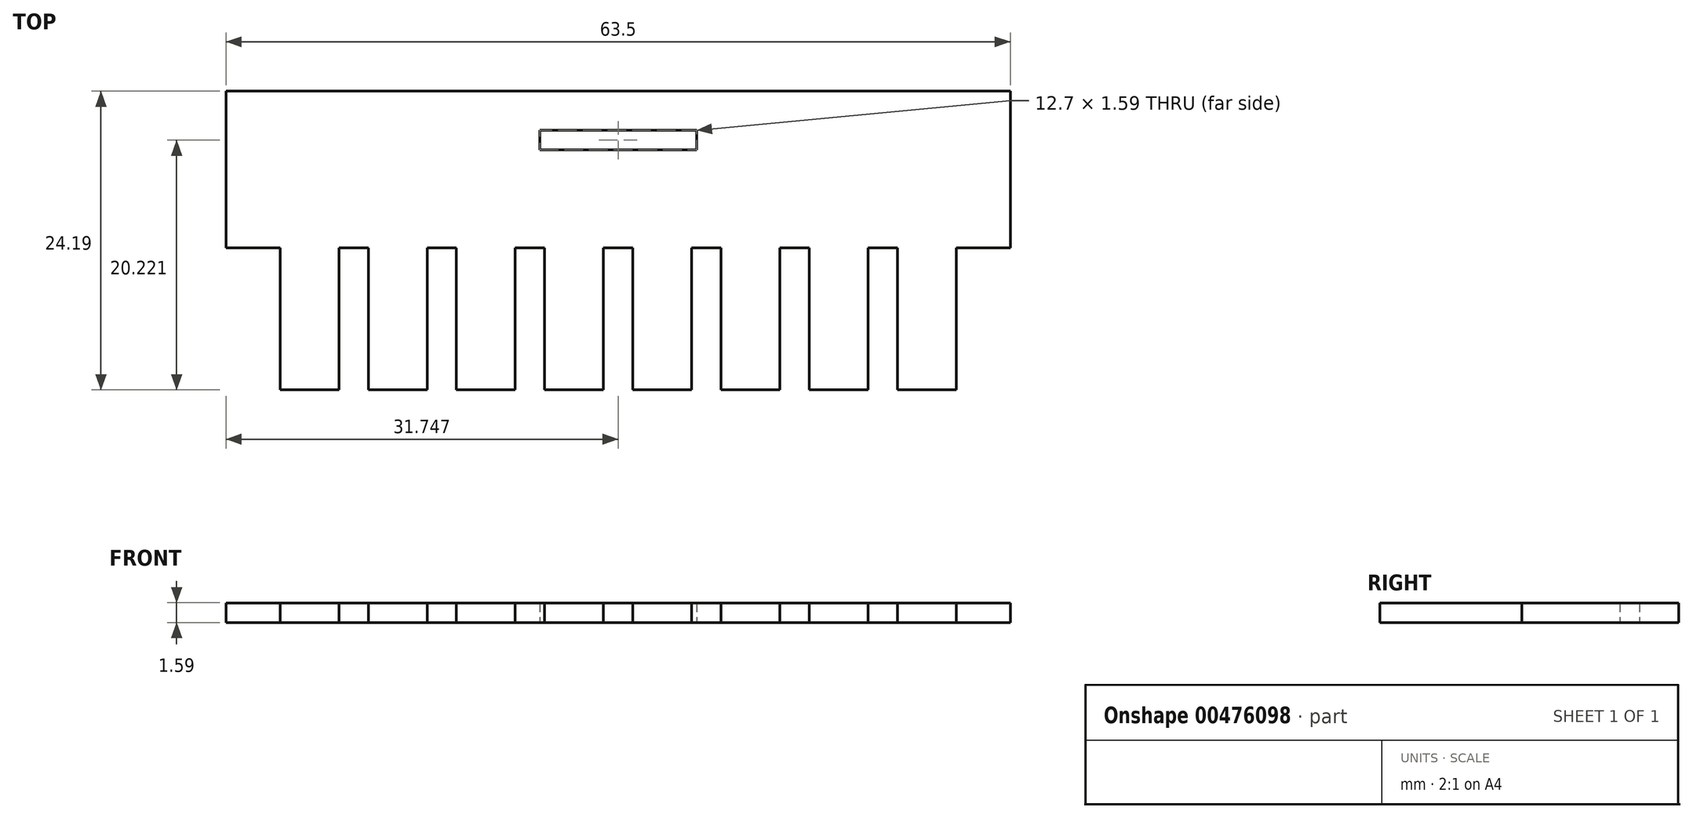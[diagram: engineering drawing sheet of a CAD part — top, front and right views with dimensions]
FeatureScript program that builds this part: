
annotation { "Feature Type Name" : "Feature", "Feature Type Description" : "" }
export const myFeature = defineFeature(function(context is Context, id is Id, definition is map)
    precondition{}
    {
        {
            var Q0;
            Q0=qCreatedBy(makeId("Top.planeOp"),FACE);
            var sketch = newSketch(context, id + "F0", { "sketchPlane" : qUnion([Q0])});
            skLineSegment(sketch, "E0.top", {"start": v(31.74, 14.04) * mm, "end": v(-31.76, 14.04) * mm});
            skPoint(sketch, "E0.middle", {"position": v(0, 0) * mm});
            skLineSegment(sketch, "E1", {"start": v(-27.38, 1.34) * mm, "end": v(-27.38, -10.15) * mm});
            skLineSegment(sketch, "E2", {"start": v(27.36, 1.34) * mm, "end": v(27.36, -10.15) * mm});
            skLineSegment(sketch, "E3", {"start": v(31.74, 14.04) * mm, "end": v(31.74, 1.34) * mm});
            skLineSegment(sketch, "E4", {"start": v(-31.76, 14.04) * mm, "end": v(-31.76, 1.34) * mm});
            skLineSegment(sketch, "E5", {"start": v(-31.76, 1.34) * mm, "end": v(-27.38, 1.34) * mm});
            skLineSegment(sketch, "E6", {"start": v(27.36, 1.34) * mm, "end": v(31.74, 1.34) * mm});
            skLineSegment(sketch, "E7", {"start": v(-27.38, -10.15) * mm, "end": v(-22.62, -10.15) * mm});
            skLineSegment(sketch, "E8", {"start": v(-22.62, -10.15) * mm, "end": v(-22.62, 1.34) * mm});
            skLineSegment(sketch, "E9", {"start": v(-22.62, 1.34) * mm, "end": v(-20.24, 1.34) * mm});
            skLineSegment(sketch, "E10", {"start": v(-20.24, 1.34) * mm, "end": v(-20.24, -10.15) * mm});
            skLineSegment(sketch, "E11", {"start": v(-20.24, -10.15) * mm, "end": v(-15.48, -10.15) * mm});
            skLineSegment(sketch, "E12", {"start": v(-15.48, -10.15) * mm, "end": v(-15.48, 1.34) * mm});
            skLineSegment(sketch, "E13", {"start": v(-15.48, 1.34) * mm, "end": v(-13.1, 1.34) * mm});
            skLineSegment(sketch, "E14", {"start": v(-13.1, 1.34) * mm, "end": v(-13.1, -10.15) * mm});
            skLineSegment(sketch, "E15", {"start": v(-13.1, -10.15) * mm, "end": v(-8.34, -10.15) * mm});
            skLineSegment(sketch, "E16", {"start": v(-8.34, -10.15) * mm, "end": v(-8.34, 1.34) * mm});
            skLineSegment(sketch, "E17", {"start": v(-8.34, 1.34) * mm, "end": v(-5.96, 1.34) * mm});
            skLineSegment(sketch, "E18", {"start": v(-5.96, 1.34) * mm, "end": v(-5.96, -10.15) * mm});
            skLineSegment(sketch, "E19", {"start": v(-5.96, -10.15) * mm, "end": v(-1.2, -10.15) * mm});
            skLineSegment(sketch, "E20", {"start": v(-1.2, -10.15) * mm, "end": v(-1.2, 1.34) * mm});
            skLineSegment(sketch, "E21", {"start": v(-1.2, 1.34) * mm, "end": v(1.18, 1.34) * mm});
            skLineSegment(sketch, "E22", {"start": v(1.18, 1.34) * mm, "end": v(1.18, -10.15) * mm});
            skLineSegment(sketch, "E23", {"start": v(1.18, -10.15) * mm, "end": v(5.94, -10.15) * mm});
            skLineSegment(sketch, "E24", {"start": v(5.94, -10.15) * mm, "end": v(5.94, 1.34) * mm});
            skLineSegment(sketch, "E25", {"start": v(5.94, 1.34) * mm, "end": v(8.31, 1.34) * mm});
            skLineSegment(sketch, "E26", {"start": v(8.31, 1.34) * mm, "end": v(8.31, -10.15) * mm});
            skLineSegment(sketch, "E27", {"start": v(8.31, -10.15) * mm, "end": v(13.08, -10.15) * mm});
            skLineSegment(sketch, "E28", {"start": v(13.08, -10.15) * mm, "end": v(13.08, 1.34) * mm});
            skLineSegment(sketch, "E29", {"start": v(13.08, 1.34) * mm, "end": v(15.45, 1.34) * mm});
            skLineSegment(sketch, "E30", {"start": v(15.45, 1.34) * mm, "end": v(15.45, -10.15) * mm});
            skLineSegment(sketch, "E31", {"start": v(27.36, -10.15) * mm, "end": v(22.6, -10.15) * mm});
            skLineSegment(sketch, "E32", {"start": v(22.6, -10.15) * mm, "end": v(22.6, 1.34) * mm});
            skLineSegment(sketch, "E33", {"start": v(20.22, 1.34) * mm, "end": v(20.22, -10.15) * mm});
            skLineSegment(sketch, "E34", {"start": v(15.45, -10.15) * mm, "end": v(20.22, -10.15) * mm});
            skLineSegment(sketch, "E35", {"start": v(20.22, 1.34) * mm, "end": v(22.6, 1.34) * mm});
            skSolve(sketch);
        }
        {
            var Q0;
            Q0=makeQuery(id+"F0.imprint","IMPRINT",FACE,{"disambiguationData":[TD([[makeQuery(id+"F0.imprint","IMPRINT",EDGE,{"derivedFrom":sQuery(id+"F0.wireOp",EDGE,"E0.top")}),1.0]])]});
            extrude(context, id + "F1", {"entities" : qUnion([Q0]), "depth" : 1.59 * mm, "offsetDistance" : 25.4 * mm});
        }
        {
            var Q0;
            Q0=makeQuery(id+"F1.opExtrude","CAP_FACE",FACE,{"disambiguationData":[OSD([sQuery(id+"F0.wireOp",EDGE,"E0.top"),sQuery(id+"F0.wireOp",EDGE,"E1"),sQuery(id+"F0.wireOp",EDGE,"E2"),sQuery(id+"F0.wireOp",EDGE,"E3"),sQuery(id+"F0.wireOp",EDGE,"E4"),sQuery(id+"F0.wireOp",EDGE,"E5"),sQuery(id+"F0.wireOp",EDGE,"E6"),sQuery(id+"F0.wireOp",EDGE,"E7"),sQuery(id+"F0.wireOp",EDGE,"E8"),sQuery(id+"F0.wireOp",EDGE,"E9"),sQuery(id+"F0.wireOp",EDGE,"E10"),sQuery(id+"F0.wireOp",EDGE,"E11"),sQuery(id+"F0.wireOp",EDGE,"E12"),sQuery(id+"F0.wireOp",EDGE,"E13"),sQuery(id+"F0.wireOp",EDGE,"E14"),sQuery(id+"F0.wireOp",EDGE,"E15"),sQuery(id+"F0.wireOp",EDGE,"E16"),sQuery(id+"F0.wireOp",EDGE,"E17"),sQuery(id+"F0.wireOp",EDGE,"E18"),sQuery(id+"F0.wireOp",EDGE,"E19"),sQuery(id+"F0.wireOp",EDGE,"E20"),sQuery(id+"F0.wireOp",EDGE,"E21"),sQuery(id+"F0.wireOp",EDGE,"E22"),sQuery(id+"F0.wireOp",EDGE,"E23"),sQuery(id+"F0.wireOp",EDGE,"E24"),sQuery(id+"F0.wireOp",EDGE,"E25"),sQuery(id+"F0.wireOp",EDGE,"E26"),sQuery(id+"F0.wireOp",EDGE,"E27"),sQuery(id+"F0.wireOp",EDGE,"E28"),sQuery(id+"F0.wireOp",EDGE,"E29"),sQuery(id+"F0.wireOp",EDGE,"E30"),sQuery(id+"F0.wireOp",EDGE,"E31"),sQuery(id+"F0.wireOp",EDGE,"E32"),sQuery(id+"F0.wireOp",EDGE,"E33"),sQuery(id+"F0.wireOp",EDGE,"E34"),sQuery(id+"F0.wireOp",EDGE,"E35")])],"isStart":true});
            var sketch = newSketch(context, id + "F2", { "sketchPlane" : qUnion([Q0])});
            skLineSegment(sketch, "E36.bottom", {"start": v(6.34, -9.28) * mm, "end": v(-6.36, -9.28) * mm});
            skLineSegment(sketch, "E36.top", {"start": v(6.34, -10.86) * mm, "end": v(-6.36, -10.86) * mm});
            skLineSegment(sketch, "E36.left", {"start": v(6.34, -9.28) * mm, "end": v(6.34, -10.86) * mm});
            skLineSegment(sketch, "E36.right", {"start": v(-6.36, -9.28) * mm, "end": v(-6.36, -10.86) * mm});
            skPoint(sketch, "E36.middle", {"position": v(-0.01, -10.07) * mm});
            skSolve(sketch);
        }
        {
            var Q0;
            Q0 = qSketchRegion(id + "F2", true);
            var Q1;
            Q1=makeQuery(id+"F1.opExtrude","CAP_FACE",FACE,{"disambiguationData":[OSD([sQuery(id+"F0.wireOp",EDGE,"E0.top"),sQuery(id+"F0.wireOp",EDGE,"E1"),sQuery(id+"F0.wireOp",EDGE,"E2"),sQuery(id+"F0.wireOp",EDGE,"E3"),sQuery(id+"F0.wireOp",EDGE,"E4"),sQuery(id+"F0.wireOp",EDGE,"E5"),sQuery(id+"F0.wireOp",EDGE,"E6"),sQuery(id+"F0.wireOp",EDGE,"E7"),sQuery(id+"F0.wireOp",EDGE,"E8"),sQuery(id+"F0.wireOp",EDGE,"E9"),sQuery(id+"F0.wireOp",EDGE,"E10"),sQuery(id+"F0.wireOp",EDGE,"E11"),sQuery(id+"F0.wireOp",EDGE,"E12"),sQuery(id+"F0.wireOp",EDGE,"E13"),sQuery(id+"F0.wireOp",EDGE,"E14"),sQuery(id+"F0.wireOp",EDGE,"E15"),sQuery(id+"F0.wireOp",EDGE,"E16"),sQuery(id+"F0.wireOp",EDGE,"E17"),sQuery(id+"F0.wireOp",EDGE,"E18"),sQuery(id+"F0.wireOp",EDGE,"E19"),sQuery(id+"F0.wireOp",EDGE,"E20"),sQuery(id+"F0.wireOp",EDGE,"E21"),sQuery(id+"F0.wireOp",EDGE,"E22"),sQuery(id+"F0.wireOp",EDGE,"E23"),sQuery(id+"F0.wireOp",EDGE,"E24"),sQuery(id+"F0.wireOp",EDGE,"E25"),sQuery(id+"F0.wireOp",EDGE,"E26"),sQuery(id+"F0.wireOp",EDGE,"E27"),sQuery(id+"F0.wireOp",EDGE,"E28"),sQuery(id+"F0.wireOp",EDGE,"E29"),sQuery(id+"F0.wireOp",EDGE,"E30"),sQuery(id+"F0.wireOp",EDGE,"E31"),sQuery(id+"F0.wireOp",EDGE,"E32"),sQuery(id+"F0.wireOp",EDGE,"E33"),sQuery(id+"F0.wireOp",EDGE,"E34"),sQuery(id+"F0.wireOp",EDGE,"E35")])],"isStart":false});
            extrude(context, id + "F3", {"entities" : qUnion([Q0]), "operationType" : NewBodyOperationType.REMOVE, "endBound" : BoundingType.UP_TO_SURFACE, "oppositeDirection" : true, "depth" : 25.4 * mm, "endBoundEntityFace" : qUnion([Q1]), "offsetDistance" : 25.4 * mm});
        }
    });
